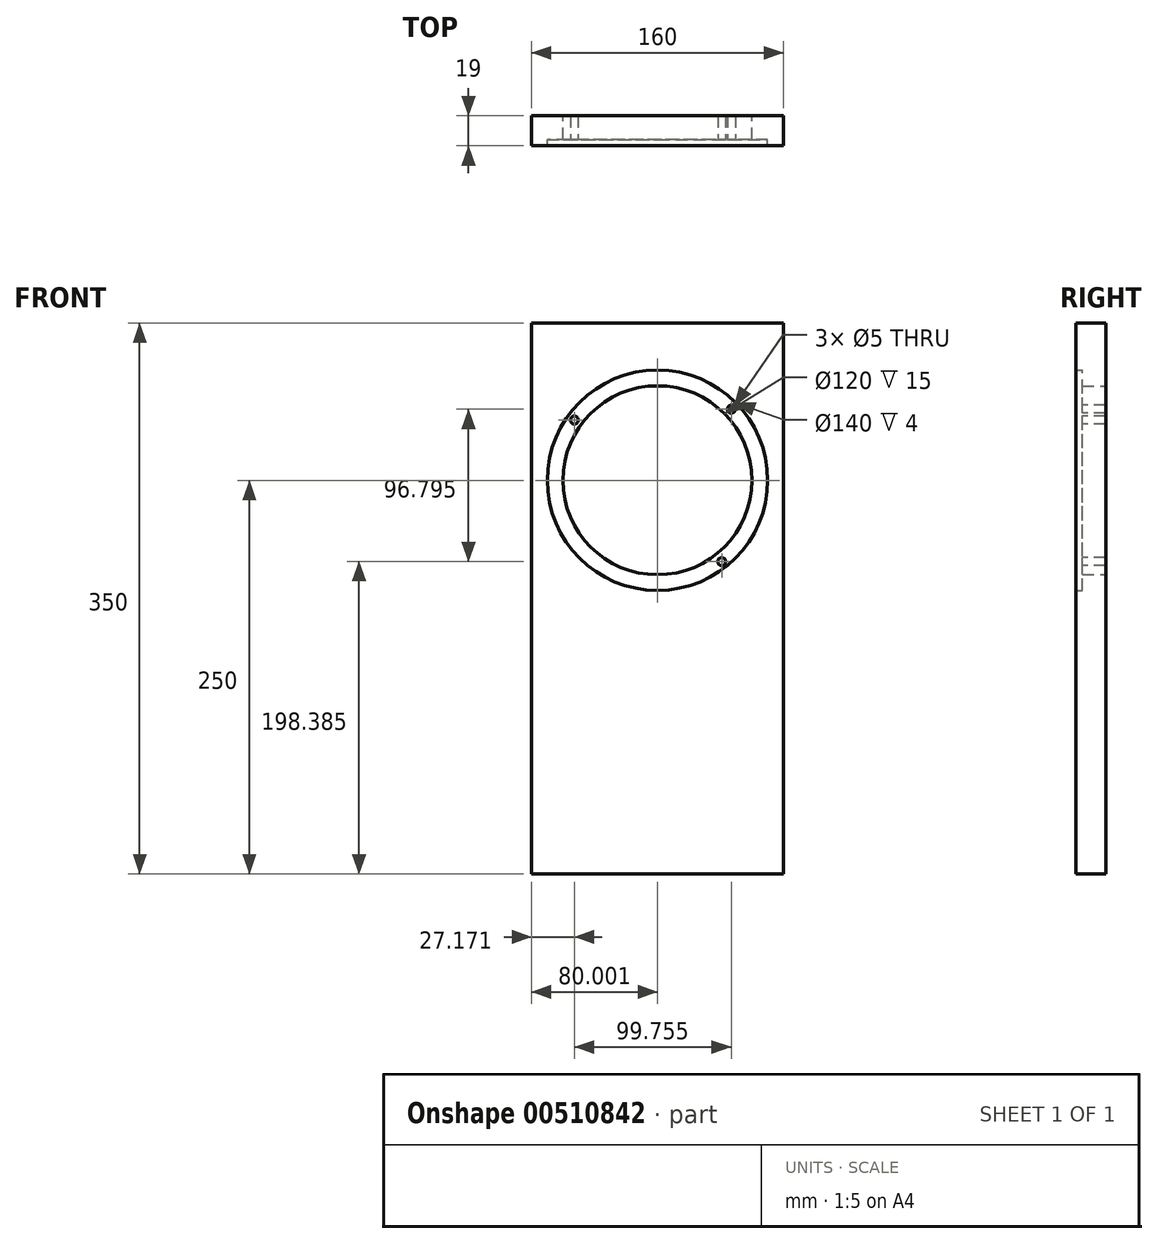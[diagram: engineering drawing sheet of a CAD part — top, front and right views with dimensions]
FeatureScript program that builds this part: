
annotation { "Feature Type Name" : "Feature", "Feature Type Description" : "" }
export const myFeature = defineFeature(function(context is Context, id is Id, definition is map)
    precondition{}
    {
        {
            var Q0;
            Q0=qCreatedBy(makeId("Front.planeOp"),FACE);
            var sketch = newSketch(context, id + "F0", { "sketchPlane" : qUnion([Q0])});
            skLineSegment(sketch, "E0.bottom", {"start": v(-53.3, 160.1) * mm, "end": v(106.7, 160.1) * mm});
            skLineSegment(sketch, "E0.top", {"start": v(-53.3, -189.9) * mm, "end": v(106.7, -189.9) * mm});
            skLineSegment(sketch, "E0.left", {"start": v(-53.3, 160.1) * mm, "end": v(-53.3, -189.9) * mm});
            skLineSegment(sketch, "E0.right", {"start": v(106.7, 160.1) * mm, "end": v(106.7, -189.9) * mm});
            skCircle(sketch, "E1", {"center": v(26.7, 60.1) * mm, "radius": 70 * mm});
            skCircle(sketch, "E2", {"center": v(26.7, 60.1) * mm, "radius": 60 * mm});
            skSolve(sketch);
        }
        {
            var Q0;
            Q0=makeQuery(id+"F0.imprint","IMPRINT",FACE,{"disambiguationData":[TD([[makeQuery(id+"F0.imprint","IMPRINT",EDGE,{"derivedFrom":sQuery(id+"F0.wireOp",EDGE,"E1")}),1.0]])]});
            extrude(context, id + "F1", {"entities" : qUnion([Q0]), "depth" : 15 * mm});
        }
        {
            var Q0;
            Q0 = qSketchRegion(id + "F0", true);
            extrude(context, id + "F2", {"entities" : qUnion([Q0]), "operationType" : NewBodyOperationType.ADD, "depth" : 19 * mm});
        }
        {
            var Q0;
            Q0=makeQuery(id+"F1.opExtrude","CAP_FACE",FACE,{"disambiguationData":[OSD([sQuery(id+"F0.wireOp",EDGE,"E1"),sQuery(id+"F0.wireOp",EDGE,"E2")])],"isStart":false});
            var sketch = newSketch(context, id + "F3", { "sketchPlane" : qUnion([Q0])});
            skPoint(sketch, "E3", {"position": v(-26.14, 98.35) * mm});
            skPoint(sketch, "E4", {"position": v(73.62, 105.28) * mm});
            skPoint(sketch, "E5", {"position": v(67.5, 8.48) * mm});
            skPoint(sketch, "E6", {"position": v(-19.93, 13.05) * mm});
            skSolve(sketch);
        }
        {
            var Q0;
            Q0=sQuery(id+"F3.wireOp",VERTEX,"E3");
            var Q1;
            Q1=sQuery(id+"F3.wireOp",VERTEX,"E4");
            var Q2;
            Q2=sQuery(id+"F3.wireOp",VERTEX,"E5");
            var Q3;
            Q3=makeQuery(id+"F1.opExtrude","SWEPT_BODY",BODY,{"disambiguationData":[OSD([sQuery(id+"F0.wireOp",EDGE,"E1"),sQuery(id+"F0.wireOp",EDGE,"E2")])]});
            hole(context, id + "F4", {"style" : HoleStyle.SIMPLE, "endStyle" : HoleEndStyle.THROUGH, "holeDiameter" : 5 * mm, "isTappedThrough" : true, "tappedDepth" : 12 * mm, "tapClearance" : 3, "locations" : qUnion([Q0, Q1, Q2]), "scope" : qUnion([Q3])});
        }
    });
